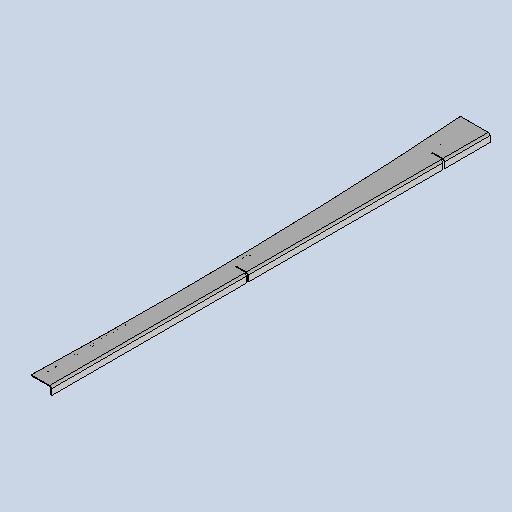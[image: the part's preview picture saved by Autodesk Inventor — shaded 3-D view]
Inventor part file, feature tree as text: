
AUTODESK INVENTOR PART (.ipt)
format: ipt  version: 2025 (Build 290162010, 162A)  size: 469,504 bytes
history: native  units: mm
features: sketch x6, other x5, sheet_metal_op x4, extrude x2, projected_geometry x2, chamfer x1, pattern_linear x1
ambient origin geometry x8: Origin, YZ Plane, XZ Plane, XY Plane, X Axis, Y Axis, Z Axis, Center Point
bodies: Body1 (feature_tree)
feature tree (21):
  sheet_metal_op  "Face2"
  sheet_metal_op  "Flange2"
  extrude  "Extrusion2"  Depth=6.0mm
  chamfer  "Chamfer2"  Distance=2.75mm
  pattern_linear  "Rectangular Pattern3"  Count1=2 Spacing1=90.0deg
  other  "Mark1"
  other  "A-Side Definition"
  extrude  "Extrusion3"  Depth=2.0mm
  sketch  "Sketch1"  dims[d16=1500.0mm d17=2700.0mm d18=2100.0mm d19=6.0mm d20=3.0mm d21=3.0mm d22=6.0mm d23=3.0mm d24=241.9mm d25=50.0mm d26=50.0mm d27=3.0mm d28=110.0mm d29=25.0mm d30=104.0mm d31=25.0mm d32=20.0mm d33=50.0mm d37=6.0mm d38=3.0mm d39=3.0mm]
  other  "Plate3"
  sketch  "Sketch3"  dims[d46=2.0mm]
  other  "Plate4"
  sheet_metal_op  "Bend2"
  sheet_metal_op  "Corner2"
  sketch  "Sketch5"  dims[d47=2.0mm]
  projected_geometry  "Projected Loop2"
  sketch  "Sketch Rectangular Pattern1"  dims[d43=3.0mm]
  sketch  "Sketch6"  dims[d48=1.0mm]
  sketch  "Sketch7"  dims[d49=4.0mm d50=2.75mm d51=20.0mm d52=90.0deg d53=2.75mm d54=8.0mm d55=2.0mm d56=2.75mm d57=500.0mm d58=500.0mm d59=500.0mm d60=500.0mm d61=500.0mm d69=1839.242466mm d70=2.0mm d71=0.0mm d72=0.0mm d76=67.563014mm d77=30.0mm d79=30.0mm d80=48.359031mm d81=30.0mm d83=250.0mm d84=40.0mm d86=550.0mm d87=10.0mm d89=10.0mm d91=274.556536mm d94=5.0mm d95=30.0mm d96=5.0mm d97=30.0mm d98=5.0mm d102=77.905549mm d104=51.799453mm d106=2.0mm d107=5.0mm d108=116.0mm d109=500.0mm d110=500.0mm d111=500.0mm d112=31.0mm d113=40.0mm d115=500.0mm d117=8.0mm d118=2.0mm d119=45.0deg d120=200.0mm d121=14.0mm d124=50.0mm d125=12.0mm d126=50.0mm d127=25.0mm d128=50.0mm d129=12.0mm d130=50.0mm d131=12.0mm d132=50.0mm d133=12.0mm d134=50.0mm d135=25.0mm d136=25.0mm d137=25.0mm d138=50.0mm d139=50.0mm d140=50.0mm d141=0.0mm d142=0.0mm d143=100.0mm]
  projected_geometry  "Projected Loop3"
  other  "Definition1"
